# Revit family: Accessory-Grab_Bars-Sterling-80001018
name_source: partatom
category: Generic Models
revit_build: Autodesk Revit 2015 (Build: 20140606_1530(x64)
units: mm (PartAtom-declared; Revit-internal decimal feet)

## types (2) — shared parameters
ADA Compliant = Yes
Assembly Code = C1030200
Date Modified = 09/13/2017
Default Elevation = 42"
Description = 18inch Grab Bar
Distance Between Supports = 12"
Height = 2 29/32"
Length = 18 1/4"
Manufacturer = Sterling
MasterFormat 1995 = 10820
MasterFormat 2004 = 10.28.13
Material = Anodized aluminum
Product Documentation Link = https://www.sterlingplumbing.com
Product Name = Grab Bar
Product Page URL = http://www.sterlingplumbing.com
URL = https://www.sterlingplumbing.com
Width = 2 1/2"

## per-type parameters (varying)
| type | Finish | Model | Type |
| N-Nickel | Kohler-Metal-N-Nickel | 80001018-N | 1 |
| V-Matte Silver | Kohler-Metal-V-Matte_Silver | 80001018-V | 2 |

## geometry (parser evidence)
native form markers: Sweep x6
no freeform markers — native parametric forms only
